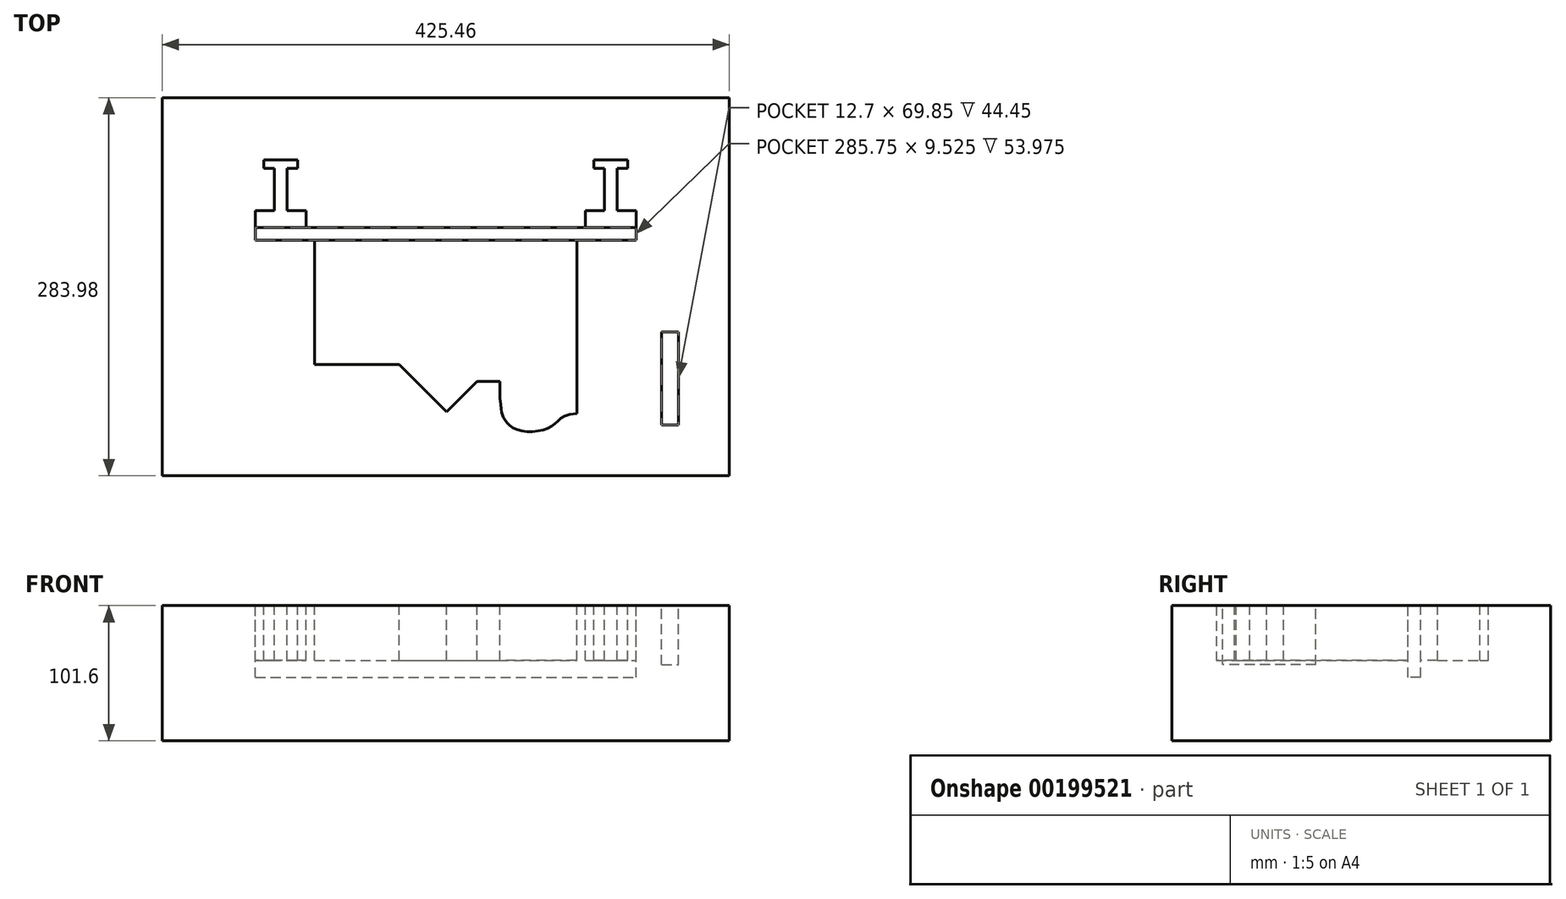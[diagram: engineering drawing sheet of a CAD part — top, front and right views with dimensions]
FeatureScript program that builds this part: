
annotation { "Feature Type Name" : "Feature", "Feature Type Description" : "" }
export const myFeature = defineFeature(function(context is Context, id is Id, definition is map)
    precondition{}
    {
        {
            var Q0;
            Q0=qCreatedBy(makeId("Top.planeOp"),FACE);
            var sketch = newSketch(context, id + "F0", { "sketchPlane" : qUnion([Q0])});
            skLineSegment(sketch, "E0.bottom", {"start": v(-212.72, 141.99) * mm, "end": v(212.73, 141.99) * mm});
            skLineSegment(sketch, "E0.top", {"start": v(-212.73, -141.99) * mm, "end": v(212.72, -141.99) * mm});
            skLineSegment(sketch, "E0.left", {"start": v(-212.72, 141.99) * mm, "end": v(-212.73, -141.99) * mm});
            skLineSegment(sketch, "E0.right", {"start": v(212.73, 141.99) * mm, "end": v(212.72, -141.99) * mm});
            skLineSegment(sketch, "E1", {"start": v(-212.73, -141.99) * mm, "end": v(212.73, 141.99) * mm, "construction": true});
            skPoint(sketch, "E2", {"position": v(0, 0) * mm});
            skSolve(sketch);
        }
        {
            var Q0;
            Q0 = qSketchRegion(id + "F0", true);
            extrude(context, id + "F1", {"entities" : qUnion([Q0]), "depth" : 101.6 * mm});
        }
        {
            var Q0;
            Q0=makeQuery(id+"F1.opExtrude","CAP_FACE",FACE,{"disambiguationData":[OSD([sQuery(id+"F0.wireOp",EDGE,"E0.bottom"),sQuery(id+"F0.wireOp",EDGE,"E0.top"),sQuery(id+"F0.wireOp",EDGE,"E0.left"),sQuery(id+"F0.wireOp",EDGE,"E0.right")])],"isStart":false});
            var sketch = newSketch(context, id + "F2", { "sketchPlane" : qUnion([Q0])});
            skLineSegment(sketch, "E3", {"start": v(104.78, 44.45) * mm, "end": v(-104.78, 44.45) * mm});
            skPoint(sketch, "E4", {"position": v(0, 44.45) * mm});
            skLineSegment(sketch, "E5", {"start": v(-104.77, 44.45) * mm, "end": v(-104.77, 57.15) * mm});
            skLineSegment(sketch, "E6", {"start": v(-104.78, 57.15) * mm, "end": v(-119.08, 57.15) * mm});
            skLineSegment(sketch, "E7", {"start": v(-119.08, 57.15) * mm, "end": v(-119.08, 88.9) * mm});
            skLineSegment(sketch, "E8", {"start": v(-119.08, 88.9) * mm, "end": v(-111.12, 88.9) * mm});
            skLineSegment(sketch, "E9", {"start": v(-111.12, 88.9) * mm, "end": v(-111.12, 95.25) * mm});
            skLineSegment(sketch, "E10", {"start": v(-111.12, 95.25) * mm, "end": v(-136.52, 95.25) * mm});
            skLineSegment(sketch, "E11", {"start": v(-136.53, 95.25) * mm, "end": v(-136.53, 88.9) * mm});
            skLineSegment(sketch, "E12", {"start": v(-136.53, 88.9) * mm, "end": v(-128.57, 88.9) * mm});
            skLineSegment(sketch, "E13", {"start": v(-128.57, 88.9) * mm, "end": v(-128.57, 57.15) * mm});
            skLineSegment(sketch, "E14", {"start": v(-128.57, 57.15) * mm, "end": v(-142.88, 57.15) * mm});
            skLineSegment(sketch, "E15", {"start": v(-142.87, 57.15) * mm, "end": v(-142.87, 34.92) * mm});
            skLineSegment(sketch, "E16", {"start": v(-142.88, 34.92) * mm, "end": v(-98.43, 34.92) * mm});
            skLineSegment(sketch, "E17", {"start": v(-98.42, 34.92) * mm, "end": v(-98.42, -58.32) * mm});
            skLineSegment(sketch, "E18", {"start": v(-98.43, -58.32) * mm, "end": v(-34.93, -58.32) * mm});
            skLineSegment(sketch, "E19", {"start": v(-34.93, -58.32) * mm, "end": v(0.64, -93.88) * mm});
            skLineSegment(sketch, "E20", {"start": v(0.64, -93.88) * mm, "end": v(23.5, -71.02) * mm});
            skLineSegment(sketch, "E21", {"start": v(23.5, -71.02) * mm, "end": v(40.65, -71.02) * mm});
            skLineSegment(sketch, "E22", {"start": v(40.65, -71.02) * mm, "end": v(40.65, -83.72) * mm});
            skLineSegment(sketch, "E23", {"start": v(40.65, -83.72) * mm, "end": v(58.42, -101.5) * mm});
            skLineSegment(sketch, "E24", {"start": v(98.43, -95.25) * mm, "end": v(98.43, 34.92) * mm});
            skLineSegment(sketch, "E25", {"start": v(0, -94.52) * mm, "end": v(0, 44.45) * mm, "construction": true});
            skLineSegment(sketch, "E26.MirrorCS", {"start": v(104.78, 44.45) * mm, "end": v(104.78, 57.15) * mm});
            skLineSegment(sketch, "E27.MirrorCS", {"start": v(104.78, 57.15) * mm, "end": v(119.08, 57.15) * mm});
            skLineSegment(sketch, "E28.MirrorCS", {"start": v(119.08, 57.15) * mm, "end": v(119.08, 88.9) * mm});
            skLineSegment(sketch, "E29.MirrorCS", {"start": v(119.08, 88.9) * mm, "end": v(111.12, 88.9) * mm});
            skLineSegment(sketch, "E30.MirrorCS", {"start": v(111.13, 88.9) * mm, "end": v(111.13, 95.25) * mm});
            skLineSegment(sketch, "E31.MirrorCS", {"start": v(111.12, 95.25) * mm, "end": v(136.52, 95.25) * mm});
            skLineSegment(sketch, "E32.MirrorCS", {"start": v(136.53, 95.25) * mm, "end": v(136.53, 88.9) * mm});
            skLineSegment(sketch, "E33.MirrorCS", {"start": v(136.53, 88.9) * mm, "end": v(128.57, 88.9) * mm});
            skLineSegment(sketch, "E34.MirrorCS", {"start": v(128.57, 88.9) * mm, "end": v(128.57, 57.15) * mm});
            skLineSegment(sketch, "E35.MirrorCS", {"start": v(128.57, 57.15) * mm, "end": v(142.88, 57.15) * mm});
            skLineSegment(sketch, "E36.MirrorCS", {"start": v(142.88, 57.15) * mm, "end": v(142.88, 34.92) * mm});
            skLineSegment(sketch, "E37.MirrorCS", {"start": v(142.88, 34.93) * mm, "end": v(98.43, 34.92) * mm});
            skLineSegment(sketch, "E38", {"start": v(136.53, 95.25) * mm, "end": v(136.53, 141.99) * mm, "construction": true});
            skLineSegment(sketch, "E39", {"start": v(98.43, -95.25) * mm, "end": v(98.43, -141.99) * mm, "construction": true});
            skLineSegment(sketch, "E40", {"start": v(-142.88, 57.15) * mm, "end": v(-212.72, 57.15) * mm, "construction": true});
            skLineSegment(sketch, "E41", {"start": v(142.88, 57.15) * mm, "end": v(212.72, 57.15) * mm, "construction": true});
            skLineSegment(sketch, "E42.bottom", {"start": v(161.93, -34.04) * mm, "end": v(174.62, -34.04) * mm});
            skLineSegment(sketch, "E42.top", {"start": v(161.93, -103.89) * mm, "end": v(174.62, -103.89) * mm});
            skLineSegment(sketch, "E42.left", {"start": v(161.93, -34.04) * mm, "end": v(161.93, -103.89) * mm});
            skLineSegment(sketch, "E42.right", {"start": v(174.62, -34.04) * mm, "end": v(174.62, -103.89) * mm});
            skFitSpline(sketch, "E43", {"points": [v(98.43, -95.25) * mm, v(78.74, -105.08) * mm, v(53.78, -107.51) * mm, v(43.43, -98.38) * mm, v(40.65, -83.72) * mm], "startDerivative": vector(-140.6, -7.9) * mm, "endDerivative": vector(-12.84, 123.2) * mm});
            skSolve(sketch);
        }
        {
            var Q0;
            Q0=makeQuery(id+"F2.imprint","IMPRINT",FACE,{"disambiguationData":[TD([[makeQuery(id+"F2.imprint","IMPRINT",EDGE,{"derivedFrom":sQuery(id+"F2.wireOp",EDGE,"E3")}),1.0]])]});
            extrude(context, id + "F3", {"entities" : qUnion([Q0]), "operationType" : NewBodyOperationType.REMOVE, "oppositeDirection" : true, "depth" : 41.27 * mm});
        }
        {
            var Q0;
            Q0=makeQuery(id+"F2.imprint","IMPRINT",FACE,{"disambiguationData":[TD([[makeQuery(id+"F2.imprint","IMPRINT",EDGE,{"derivedFrom":sQuery(id+"F2.wireOp",EDGE,"E42.bottom")}),-1.0]])]});
            extrude(context, id + "F4", {"entities" : qUnion([Q0]), "operationType" : NewBodyOperationType.REMOVE, "oppositeDirection" : true, "depth" : 44.45 * mm});
        }
        {
            var Q0;
            Q0=makeQuery(id+"F3.boolean.opBoolean","COPY",FACE,{"derivedFrom":makeQuery(id+"F3.opExtrude","CAP_FACE",FACE,{"disambiguationData":[OSD([sQuery(id+"F2.wireOp",EDGE,"E3"),sQuery(id+"F2.wireOp",EDGE,"E5"),sQuery(id+"F2.wireOp",EDGE,"E6"),sQuery(id+"F2.wireOp",EDGE,"E7"),sQuery(id+"F2.wireOp",EDGE,"E8"),sQuery(id+"F2.wireOp",EDGE,"E9"),sQuery(id+"F2.wireOp",EDGE,"E10"),sQuery(id+"F2.wireOp",EDGE,"E11"),sQuery(id+"F2.wireOp",EDGE,"E12"),sQuery(id+"F2.wireOp",EDGE,"E13"),sQuery(id+"F2.wireOp",EDGE,"E14"),sQuery(id+"F2.wireOp",EDGE,"E15"),sQuery(id+"F2.wireOp",EDGE,"E16"),sQuery(id+"F2.wireOp",EDGE,"E17"),sQuery(id+"F2.wireOp",EDGE,"E18"),sQuery(id+"F2.wireOp",EDGE,"E19"),sQuery(id+"F2.wireOp",EDGE,"E20"),sQuery(id+"F2.wireOp",EDGE,"E21"),sQuery(id+"F2.wireOp",EDGE,"E22"),sQuery(id+"F2.wireOp",EDGE,"E23"),sQuery(id+"F2.wireOp",EDGE,"3f082c9e-4d98-4ee7-9170-67e18480f00b"),sQuery(id+"F2.wireOp",EDGE,"E24"),sQuery(id+"F2.wireOp",EDGE,"E26.MirrorCS"),sQuery(id+"F2.wireOp",EDGE,"E27.MirrorCS"),sQuery(id+"F2.wireOp",EDGE,"E28.MirrorCS"),sQuery(id+"F2.wireOp",EDGE,"E29.MirrorCS"),sQuery(id+"F2.wireOp",EDGE,"E30.MirrorCS"),sQuery(id+"F2.wireOp",EDGE,"E31.MirrorCS"),sQuery(id+"F2.wireOp",EDGE,"E32.MirrorCS"),sQuery(id+"F2.wireOp",EDGE,"E33.MirrorCS"),sQuery(id+"F2.wireOp",EDGE,"E34.MirrorCS"),sQuery(id+"F2.wireOp",EDGE,"E35.MirrorCS"),sQuery(id+"F2.wireOp",EDGE,"E36.MirrorCS"),sQuery(id+"F2.wireOp",EDGE,"E37.MirrorCS")])],"isStart":false})});
            var sketch = newSketch(context, id + "F5", { "sketchPlane" : qUnion([Q0])});
            skLineSegment(sketch, "E44.bottom", {"start": v(-142.87, 34.92) * mm, "end": v(142.88, 34.92) * mm});
            skLineSegment(sketch, "E44.top", {"start": v(-142.87, 44.45) * mm, "end": v(142.88, 44.45) * mm});
            skLineSegment(sketch, "E44.left", {"start": v(-142.87, 34.92) * mm, "end": v(-142.87, 44.45) * mm});
            skLineSegment(sketch, "E44.right", {"start": v(142.88, 34.92) * mm, "end": v(142.88, 44.45) * mm});
            skSolve(sketch);
        }
        {
            var Q0;
            {var subQ2=sQuery(id+"F5.wireOp",EDGE,"E44.left");Q0=makeQuery(id+"F5.imprint","IMPRINT",FACE,{"disambiguationData":[TD([[makeQuery(id+"F5.imprint","IMPRINT",EDGE,{"derivedFrom":subQ2}),1.0]])]});}
            extrude(context, id + "F6", {"entities" : qUnion([Q0]), "operationType" : NewBodyOperationType.REMOVE, "oppositeDirection" : true, "depth" : 12.7 * mm});
        }
    });
